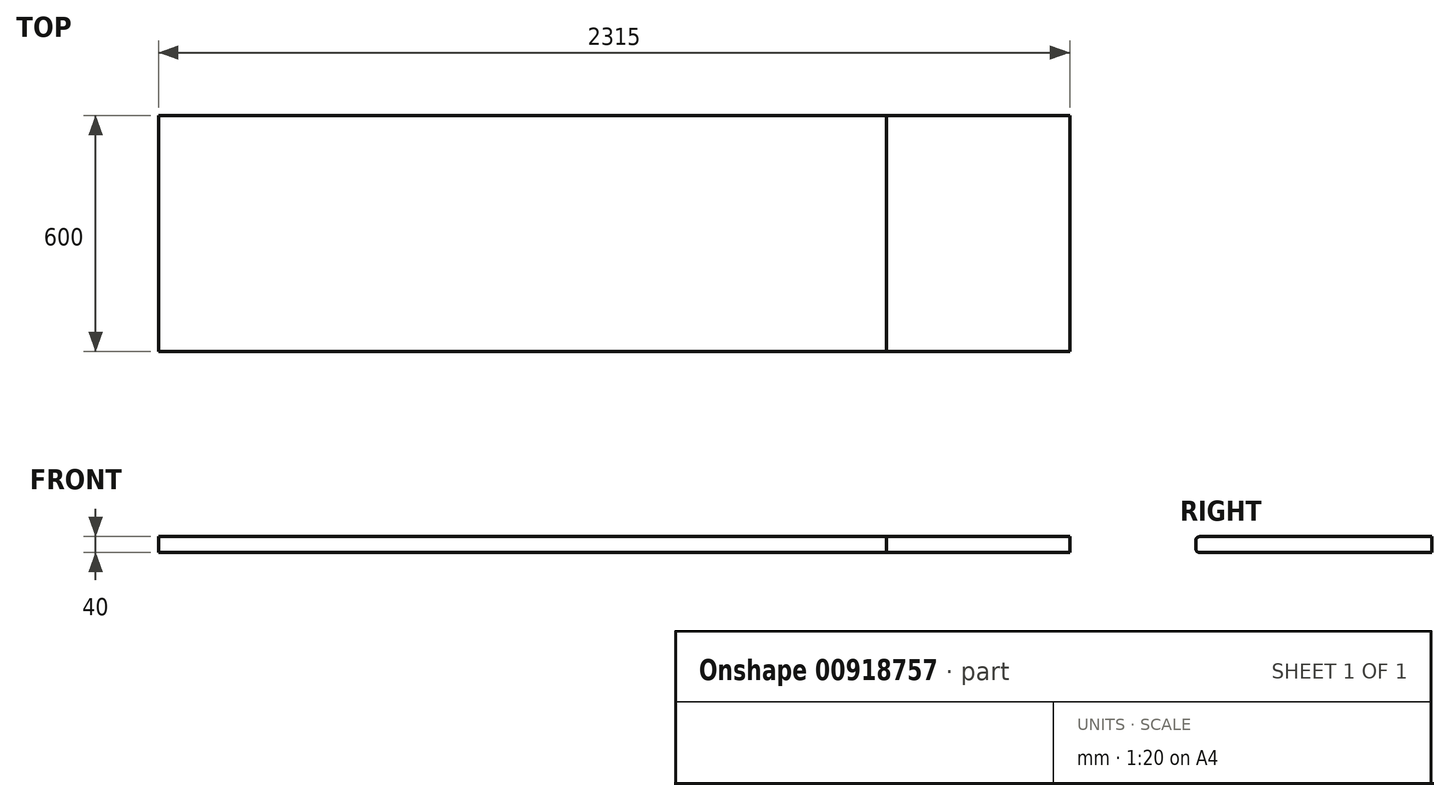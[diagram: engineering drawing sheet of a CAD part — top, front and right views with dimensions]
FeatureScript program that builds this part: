
annotation { "Feature Type Name" : "Feature", "Feature Type Description" : "" }
export const myFeature = defineFeature(function(context is Context, id is Id, definition is map)
    precondition{}
    {
        {
            var Q0;
            Q0=qCreatedBy(makeId("Top.planeOp"),FACE);
            var sketch = newSketch(context, id + "F0", { "sketchPlane" : qUnion([Q0])});
            skLineSegment(sketch, "E0.bottom", {"start": v(0, 0) * mm, "end": v(1850, 0) * mm});
            skLineSegment(sketch, "E0.top", {"start": v(0, 600) * mm, "end": v(1850, 600) * mm});
            skLineSegment(sketch, "E0.left", {"start": v(0, 0) * mm, "end": v(0, 600) * mm});
            skLineSegment(sketch, "E0.right", {"start": v(1850, 0) * mm, "end": v(1850, 600) * mm});
            skSolve(sketch);
        }
        {
            var Q0;
            Q0 = qSketchRegion(id + "F0", true);
            extrude(context, id + "F1", {"entities" : qUnion([Q0]), "depth" : 40 * mm, "offsetDistance" : 25 * mm});
        }
        {
            var Q0;
            Q0=makeQuery(id+"F1.opExtrude","CAP_EDGE",EDGE,{"disambiguationData":[OSD([sQuery(id+"F0.wireOp",EDGE,"E0.bottom")])],"isStart":false});
            var Q1;
            Q1=makeQuery(id+"F1.opExtrude","CAP_EDGE",EDGE,{"disambiguationData":[OSD([sQuery(id+"F0.wireOp",EDGE,"E0.bottom")])],"isStart":true});
            fillet(context, id + "F2", {"entities" : qUnion([Q0, Q1]), "radius" : 10 * mm, "tangentPropagation" : true, "allowEdgeOverflow" : false});
        }
        {
            var Q0;
            Q0=makeQuery(id+"F1.opExtrude","SWEPT_FACE",FACE,{"disambiguationData":[OSD([sQuery(id+"F0.wireOp",EDGE,"E0.right")])]});
            extrude(context, id + "F3", {"entities" : qUnion([Q0]), "depth" : 465 * mm, "offsetDistance" : 25 * mm});
        }
    });
